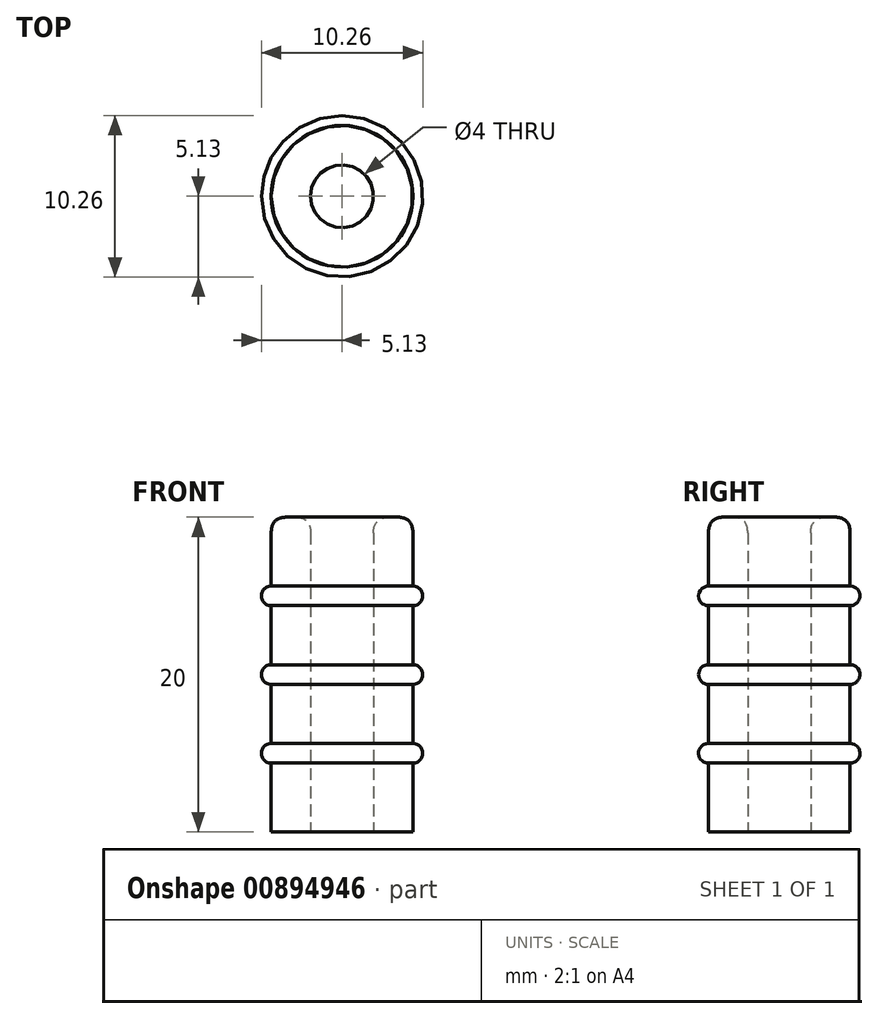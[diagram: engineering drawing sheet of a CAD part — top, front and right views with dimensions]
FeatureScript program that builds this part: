
annotation { "Feature Type Name" : "Feature", "Feature Type Description" : "" }
export const myFeature = defineFeature(function(context is Context, id is Id, definition is map)
    precondition{}
    {
        {
            var Q0;
            Q0=qCreatedBy(makeId("Top.planeOp"),FACE);
            var sketch = newSketch(context, id + "F0", { "sketchPlane" : qUnion([Q0])});
            skCircle(sketch, "E0", {"center": v(0, 0) * mm, "radius": 2 * mm});
            skCircle(sketch, "E1", {"center": v(0, 0) * mm, "radius": 3.6 * mm});
            skSolve(sketch);
        }
        {
            var Q0;
            Q0=makeQuery(id+"F0.imprint","IMPRINT",FACE,{"disambiguationData":[TD([[makeQuery(id+"F0.imprint","IMPRINT",EDGE,{"derivedFrom":sQuery(id+"F0.wireOp",EDGE,"E0")}),-1.0]])]});
            cPlane(context, id + "F1", {"entities" : qUnion([Q0]), "cplaneType" : CPlaneType.OFFSET, "offset" : 6 * mm, "width" : 150 * mm, "height" : 150 * mm});
        }
        {
            var Q0;
            Q0=qCreatedBy(makeId("Front.planeOp"),FACE);
            var sketch = newSketch(context, id + "F2", { "sketchPlane" : qUnion([Q0])});
            skLineSegment(sketch, "E2", {"start": v(0, 0) * mm, "end": v(0, 6) * mm});
            skLineSegment(sketch, "E3", {"start": v(0, 6) * mm, "end": v(0, 26) * mm});
            skLineSegment(sketch, "E4", {"start": v(0, 26) * mm, "end": v(2, 26) * mm});
            skLineSegment(sketch, "E5", {"start": v(2, 26) * mm, "end": v(4.5, 26) * mm});
            skLineSegment(sketch, "E6", {"start": v(2, 26) * mm, "end": v(2, 6) * mm});
            skLineSegment(sketch, "E7", {"start": v(2, 6) * mm, "end": v(4.5, 6) * mm});
            skLineSegment(sketch, "E8", {"start": v(4.5, 26) * mm, "end": v(4.5, 21.63) * mm});
            skLineSegment(sketch, "E9", {"start": v(4.5, 20.38) * mm, "end": v(4.5, 16.62) * mm});
            skLineSegment(sketch, "E10", {"start": v(4.5, 15.38) * mm, "end": v(4.5, 11.62) * mm});
            skArc(sketch, "E11", {"start": v(4.5, 20.38) * mm, "mid": v(5.12, 21) * mm, "end": v(4.5, 21.63) * mm});
            skArc(sketch, "E12", {"start": v(4.5, 15.38) * mm, "mid": v(5.12, 16) * mm, "end": v(4.5, 16.62) * mm});
            skArc(sketch, "E13", {"start": v(4.5, 10.37) * mm, "mid": v(5.12, 11) * mm, "end": v(4.5, 11.62) * mm});
            skLineSegment(sketch, "E14.trimOffspring", {"start": v(4.5, 10.37) * mm, "end": v(4.5, 6) * mm});
            skSolve(sketch);
        }
        {
            var Q0;
            Q0=makeQuery(id+"F2.imprint","IMPRINT",FACE,{"disambiguationData":[TD([[makeQuery(id+"F2.imprint","IMPRINT",EDGE,{"derivedFrom":sQuery(id+"F2.wireOp",EDGE,"E5")}),-1.0]])]});
            var Q1;
            Q1=sQuery(id+"F2.wireOp",EDGE,"E3");
            revolve(context, id + "F3", {"surfaceOperationType" : NewSurfaceOperationType.NEW, "entities" : qUnion([Q0]), "axis" : qUnion([Q1]), "revolveType" : RevolveType.FULL});
        }
        {
            var Q0;
            Q0=makeQuery(id+"F3.opRevolve","SWEPT_EDGE",EDGE,{"disambiguationData":[OSD([sQuery(id+"F2.wireOp",EDGE,"E5"),sQuery(id+"F2.wireOp",EDGE,"E8")])]});
            var Q1;
            Q1=makeQuery(id+"F3.opRevolve","SWEPT_EDGE",EDGE,{"disambiguationData":[OSD([sQuery(id+"F2.wireOp",EDGE,"E5"),sQuery(id+"F2.wireOp",EDGE,"E6")])]});
            fillet(context, id + "F4", {"entities" : qUnion([Q0, Q1]), "radius" : 1 * mm, "tangentPropagation" : true, "rho" : 0.5, "crossSection" : FilletCrossSection.CONIC, "allowEdgeOverflow" : false});
        }
    });
